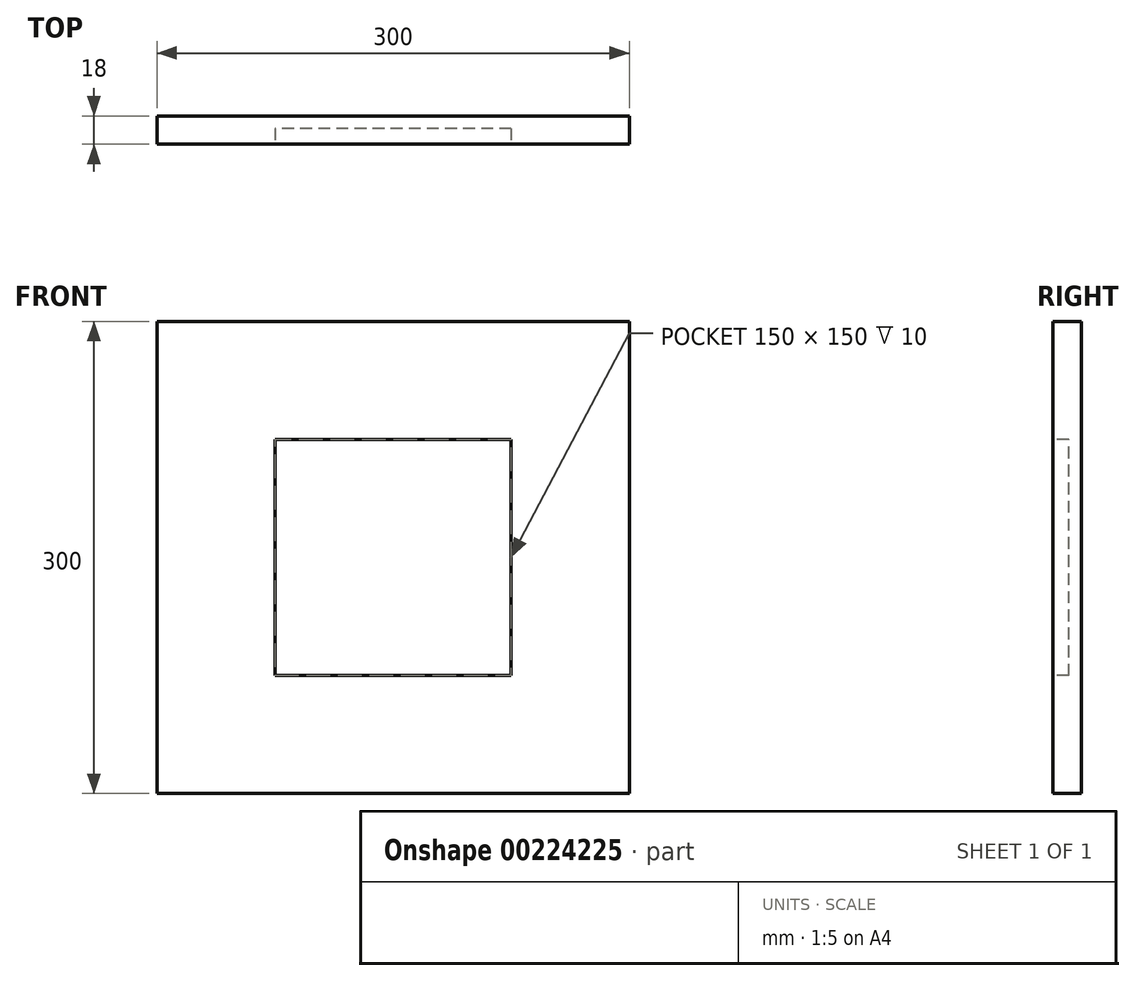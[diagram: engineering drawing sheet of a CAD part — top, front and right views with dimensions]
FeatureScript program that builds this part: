
annotation { "Feature Type Name" : "Feature", "Feature Type Description" : "" }
export const myFeature = defineFeature(function(context is Context, id is Id, definition is map)
    precondition{}
    {
        {
            var Q0;
            Q0=qCreatedBy(makeId("Front.planeOp"),FACE);
            var sketch = newSketch(context, id + "F0", { "sketchPlane" : qUnion([Q0])});
            skLineSegment(sketch, "E0.bottom", {"start": v(150, -150) * mm, "end": v(-150, -150) * mm});
            skLineSegment(sketch, "E0.top", {"start": v(150, 150) * mm, "end": v(-150, 150) * mm});
            skLineSegment(sketch, "E0.left", {"start": v(150, -150) * mm, "end": v(150, 150) * mm});
            skLineSegment(sketch, "E0.right", {"start": v(-150, -150) * mm, "end": v(-150, 150) * mm});
            skPoint(sketch, "E0.middle", {"position": v(0, 0) * mm});
            skSolve(sketch);
        }
        {
            var Q0;
            Q0 = qSketchRegion(id + "F0", true);
            extrude(context, id + "F1", {"entities" : qUnion([Q0]), "oppositeDirection" : true, "depth" : 18 * mm});
        }
        {
            var Q0;
            Q0=makeQuery(id+"F1.opExtrude","CAP_FACE",FACE,{"disambiguationData":[OSD([sQuery(id+"F0.wireOp",EDGE,"E0.bottom"),sQuery(id+"F0.wireOp",EDGE,"E0.top"),sQuery(id+"F0.wireOp",EDGE,"E0.left"),sQuery(id+"F0.wireOp",EDGE,"E0.right")])],"isStart":true});
            var sketch = newSketch(context, id + "F2", { "sketchPlane" : qUnion([Q0])});
            skLineSegment(sketch, "E1.bottom", {"start": v(75, -75) * mm, "end": v(-75, -75) * mm});
            skLineSegment(sketch, "E1.top", {"start": v(75, 75) * mm, "end": v(-75, 75) * mm});
            skLineSegment(sketch, "E1.left", {"start": v(75, -75) * mm, "end": v(75, 75) * mm});
            skLineSegment(sketch, "E1.right", {"start": v(-75, -75) * mm, "end": v(-75, 75) * mm});
            skPoint(sketch, "E1.middle", {"position": v(0, 0) * mm});
            skSolve(sketch);
        }
        {
            var Q0;
            Q0 = qSketchRegion(id + "F2", true);
            extrude(context, id + "F3", {"entities" : qUnion([Q0]), "operationType" : NewBodyOperationType.REMOVE, "oppositeDirection" : true, "depth" : 10 * mm});
        }
    });
